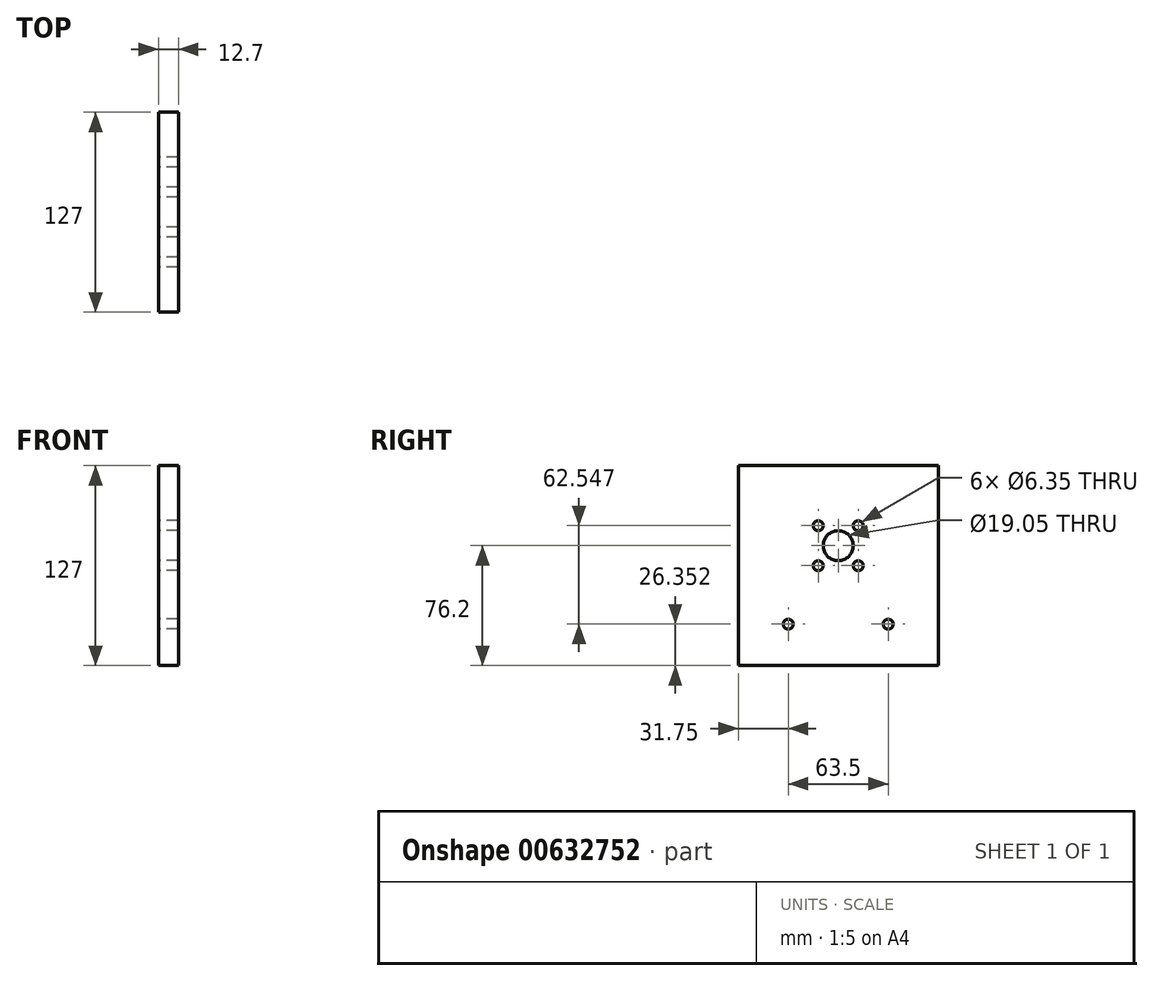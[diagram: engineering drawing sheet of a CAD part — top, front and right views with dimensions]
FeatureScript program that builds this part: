
annotation { "Feature Type Name" : "Feature", "Feature Type Description" : "" }
export const myFeature = defineFeature(function(context is Context, id is Id, definition is map)
    precondition{}
    {
        {
            var Q0;
            Q0=qCreatedBy(makeId("Front.planeOp"),FACE);
            var sketch = newSketch(context, id + "F0", { "sketchPlane" : qUnion([Q0])});
            skLineSegment(sketch, "E0.bottom", {"start": v(-6.35, 63.5) * mm, "end": v(6.35, 63.5) * mm});
            skLineSegment(sketch, "E0.top", {"start": v(-6.35, -63.5) * mm, "end": v(6.35, -63.5) * mm});
            skLineSegment(sketch, "E0.left", {"start": v(-6.35, 63.5) * mm, "end": v(-6.35, -63.5) * mm});
            skLineSegment(sketch, "E0.right", {"start": v(6.35, 63.5) * mm, "end": v(6.35, -63.5) * mm});
            skPoint(sketch, "E0.middle", {"position": v(0, 0) * mm});
            skSolve(sketch);
        }
        {
            var Q0;
            Q0 = qSketchRegion(id + "F0", true);
            extrude(context, id + "F1", {"entities" : qUnion([Q0]), "endBound" : BoundingType.SYMMETRIC, "depth" : 127 * mm, "offsetDistance" : 25.4 * mm});
        }
        {
            var Q0;
            Q0=makeQuery(id+"F1.opExtrude","SWEPT_FACE",FACE,{"disambiguationData":[OSD([sQuery(id+"F0.wireOp",EDGE,"E0.left")])]});
            var sketch = newSketch(context, id + "F2", { "sketchPlane" : qUnion([Q0])});
            skPoint(sketch, "E1", {"position": v(0, 12.7) * mm});
            skCircle(sketch, "E2", {"center": v(0, 12.7) * mm, "radius": 9.53 * mm});
            skPoint(sketch, "E3", {"position": v(-12.7, 25.4) * mm});
            skPoint(sketch, "E4", {"position": v(12.7, 25.4) * mm});
            skPoint(sketch, "E5", {"position": v(12.7, 0) * mm});
            skPoint(sketch, "E6", {"position": v(-12.7, 0) * mm});
            skCircle(sketch, "E7", {"center": v(-12.7, 25.4) * mm, "radius": 3.18 * mm});
            skCircle(sketch, "E8", {"center": v(-12.7, 0) * mm, "radius": 3.18 * mm});
            skCircle(sketch, "E9", {"center": v(12.7, 0) * mm, "radius": 3.18 * mm});
            skCircle(sketch, "E10", {"center": v(12.7, 25.4) * mm, "radius": 3.18 * mm});
            skPoint(sketch, "E11", {"position": v(-31.75, -37.15) * mm});
            skPoint(sketch, "E12", {"position": v(31.75, -37.15) * mm});
            skCircle(sketch, "E13", {"center": v(-31.75, -37.15) * mm, "radius": 3.18 * mm});
            skCircle(sketch, "E14", {"center": v(31.75, -37.15) * mm, "radius": 3.18 * mm});
            skSolve(sketch);
        }
        {
            var Q0;
            Q0 = qSketchRegion(id + "F2", true);
            extrude(context, id + "F3", {"entities" : qUnion([Q0]), "operationType" : NewBodyOperationType.REMOVE, "endBound" : BoundingType.THROUGH_ALL, "oppositeDirection" : true, "depth" : 25.4 * mm, "offsetDistance" : 25.4 * mm});
        }
    });
